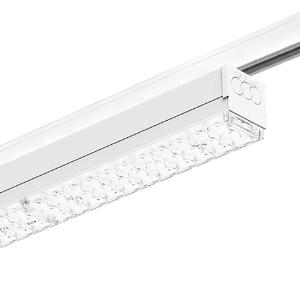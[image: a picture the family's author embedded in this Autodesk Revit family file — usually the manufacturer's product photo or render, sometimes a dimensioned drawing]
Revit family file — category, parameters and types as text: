
# Revit family: 3f_filippi_-_3f_zeta_track_l_ampio_3f_filippi_-_47132_-_3f_zeta_tk_l_30_ampio_l1194
name_source: partatom
category: Lighting Fixtures
units: mm (PartAtom-declared; Revit-internal decimal feet)

## family parameters
Cut with Voids When Loaded = No
Host = Face
Light Source = No
Part Type = Normal
Room Calculation Point = No
Round Connector Dimension = Use Diameter
Shared = No

## types (1)
- 3F Filippi - 3F Zeta Track L Ampio (1 x LED, 5498 lm, 31 W, 4000 K)
    Apparent Load = 31 VA
    Approval mark = CE
    CIE Flux Codes = 61 95 99 99 100
    Color Rendering = 80
    Color Temperature = 4000 K
    Control Gear = Electronic ballast
    Default Elevation = 1800 mm
    Description = ILLUMINOTECHNICAL
Luminous efficiency 100% (DLOR 99%, ULOR 1%).
Initial luminous flux of the luminaire 5498 lm.
Symmetric wide direct distribution.
Installation Interdistance Transv.D = 1.39 x hu - Long.D = 1.43 x hu.
Tabular UGR (CIE 117 - 4H-8H; S=0.25H; 70/50/20): RUG 21.7 - 22.4.
Beam angle: 102° - 103°.
Luminous efficacy 177 lm/W.
Lifetime (L93/B10): 30000 h. (tq+25°C)
Lifetime (L90/B10): 50000 h. (tq+25°C)
Lifetime (L85/B10): 80000 h. (tq+25°C)
Lifetime (L80/B10): 100000 h. (tq+25°C)
Sudden decreased luminous flux after 50000 hours: 0% (C0).
Photobiological safety in compliance with IEC/TR 62778: RG0 risk exempt, (IEC 62471).
In compliance with IEC/EN 62722-2-1 - IEC/EN 62717 standards.

SOURCE
Linear LED module 30W/840.
Energy efficiency class (UE 2019/2020 - UE 2019/2015): C.
CIE 13.3 Colour rendering index: CRI >80 (R9 <50%).
IES TM-30 Fidelity Index: Rf = 84 Rg = 95.
CCT nominal colour temperature 4000 K.
Colour initial tolerance (MacAdam): SDCM 3.

MECHANICAL
Housing in hot-galvanised steel, painted in white polyester, obtained through rolling process with adapters to busbar in white polycarbonate.
Mechanical truck adapter.
Light unit in hot-galvanised steel, painted in white polyester base with fixing springs and retractable safety hooks in stainless steel.
Lenses for wide distribution, in transparent methacrylate (PMMA) with external flat surface.
End caps in white polycarbonate.
Luminaire with limited surface temperature. - D - (EN 60598-2-24)
Dimensions: 1194x62 mm, height 67 mm. Weight 2.665 kg.
IP40 protection degree.
Mechanical strength to impacts IK06 (1 joule).
Glow-wire test resistance 650°C.

ELECTRICAL
Halogen Free electronic wiring 230V-50/60Hz, power factor 0.90, THD <25%, constant output current, class I, 1 driver.
Power of the luminaire 31 W.
ENEC - CE.
SAFE FLICKER: PstLM=<1 and SVM=<0.4 (IEC TR 61547-1 and IEC TR 63158), to ensure a more comfortable and safe light.
Ambient temperature from 0°C to +25°C.
Temperature class T6 max 85°C.
Truck adapter, 4-way.
Relative humidity UR: <85%.

INSTALLATION
Track.
This product is suitable for installation on a 3-phase electrified busbar "Binario 3F".

APPLICATIONS
Environments: architectural, commercial, transit areas, cornices, boards.

WARNING
Luminaire designed for disposal/recycling at end-of-life.
Replaceable (LED only) light source by a professional. Replaceable control gear by a professional.
    Height = 67 mm
    Lamp = 1 x LED
    Lamp Light Flux = 5498 lm
    Lamp Power = 31 W
    Lamp count = 1
    Length = 1194 mm
    Lifetime = 50000 h
    Luminous efficacy = 177 lm/W
    Manufacturer = 3F Filippi
    ModVariant = No
    Model = 3F Filippi - 47132 - 3F Zeta TK L 30 AMPIO L1194
    Mounting Place = Ceiling
    Mounting Type = Rail mounted
    Number of Poles = 1
    OnlyDefault = Yes
    Power Factor = 1
    Product Name = 3F Filippi - 3F Zeta Track L Ampio
    Product group = track mounted spotlight
    ProductGroupID = 12
    Protection Class = Protection class I
    Protection Degree = IP 40
    RLX_Detail_Level = 1
    RLX_Emergency_Light_Flux = 0 lm
    RLX_Emergency_Type = 0
    RLX_Emergency_Type_DB = No
    RlxData = <blob elided: 132225 chars, md5=8920e869>
    Socket = socket
    Standby Power = 0 W
    System Light Flux = 5498 lm
    System Power = 31 W
    Type Comments = Product without accessories
    Type Image = 3ffilippi_3f_zeta_track_l_ampio.jpg
    URL = http://relux.com
    VarID = ---
    Voltage = 0 V
    Weight = 0.00 kg
    Width = 62 mm  [stored 0.203412 ft]

note: [stored X ft] marks values corroborated as IEEE doubles in the binary element streams (Revit-internal decimal feet)

## geometry (parser evidence)
native form markers: Blend x4, Sweep x10
no freeform markers — native parametric forms only
